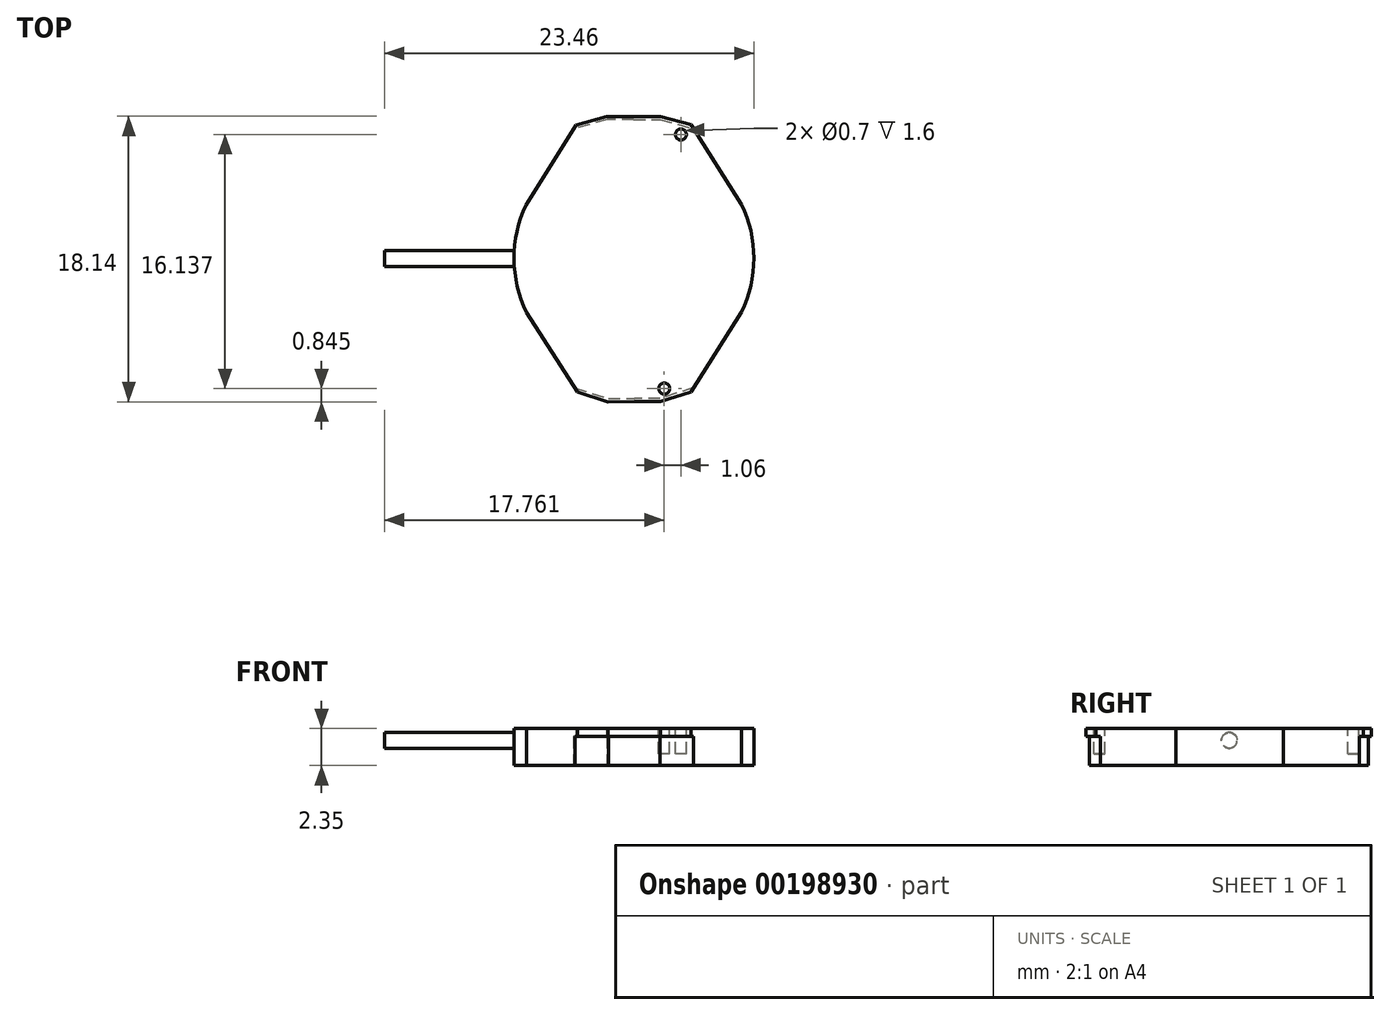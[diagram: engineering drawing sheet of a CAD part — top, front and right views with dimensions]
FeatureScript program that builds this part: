
annotation { "Feature Type Name" : "Feature", "Feature Type Description" : "" }
export const myFeature = defineFeature(function(context is Context, id is Id, definition is map)
    precondition{}
    {
        {
            var Q0;
            Q0=qCreatedBy(makeId("Top.planeOp"),FACE);
            var sketch = newSketch(context, id + "F0", { "sketchPlane" : qUnion([Q0])});
            skLineSegment(sketch, "E0", {"start": v(0, 0) * mm, "end": v(0, 18.2) * mm, "construction": true});
            skLineSegment(sketch, "E1", {"start": v(10.82, 18.2) * mm, "end": v(12.53, 18.2) * mm});
            skLineSegment(sketch, "E2", {"start": v(12.53, 18.2) * mm, "end": v(14.46, 17.67) * mm});
            skLineSegment(sketch, "E3", {"start": v(14.46, 17.67) * mm, "end": v(17.68, 12.6) * mm});
            skLineSegment(sketch, "E4", {"start": v(17.68, 5.76) * mm, "end": v(14.46, 0.7) * mm});
            skLineSegment(sketch, "E5", {"start": v(14.46, 0.7) * mm, "end": v(12.53, 0.07) * mm});
            skLineSegment(sketch, "E6", {"start": v(12.53, 0.07) * mm, "end": v(10.86, 0.07) * mm});
            skPoint(sketch, "E7.end.orphan", {"position": v(9.1, 18.2) * mm});
            skArc(sketch, "E8", {"start": v(17.68, 5.76) * mm, "mid": v(18.46, 9.19) * mm, "end": v(17.68, 12.6) * mm});
            skLineSegment(sketch, "E9.MirrorCS", {"start": v(10.82, 18.2) * mm, "end": v(9.1, 18.2) * mm});
            skLineSegment(sketch, "E10.MirrorCS", {"start": v(9.1, 18.2) * mm, "end": v(7.17, 17.65) * mm});
            skLineSegment(sketch, "E11.MirrorCS", {"start": v(7.17, 17.65) * mm, "end": v(3.98, 12.57) * mm});
            skArc(sketch, "E12.MirrorCS", {"start": v(4.02, 5.73) * mm, "mid": v(3.22, 9.15) * mm, "end": v(3.98, 12.57) * mm});
            skLineSegment(sketch, "E13.MirrorCS", {"start": v(4.02, 5.73) * mm, "end": v(7.26, 0.68) * mm});
            skLineSegment(sketch, "E14.MirrorCS", {"start": v(7.26, 0.68) * mm, "end": v(9.2, 0.06) * mm});
            skLineSegment(sketch, "E15.MirrorCS", {"start": v(9.2, 0.06) * mm, "end": v(10.86, 0.07) * mm});
            skPoint(sketch, "E16.MirrorCS.end.orphan", {"position": v(4.02, 5.73) * mm});
            skPoint(sketch, "E16.MirrorCS.start.orphan", {"position": v(3.98, 12.57) * mm});
            skSolve(sketch);
        }
        {
            var Q0;
            Q0=makeQuery(id+"F0.imprint","IMPRINT",FACE,{"disambiguationData":[TD([[makeQuery(id+"F0.imprint","IMPRINT",EDGE,{"derivedFrom":sQuery(id+"F0.wireOp",EDGE,"E1")}),-1.0]])]});
            extrude(context, id + "F1", {"entities" : qUnion([Q0]), "depth" : 2.35 * mm});
        }
        {
            var Q0;
            Q0=qCreatedBy(makeId("Right.planeOp"),FACE);
            var sketch = newSketch(context, id + "F2", { "sketchPlane" : qUnion([Q0])});
            skLineSegment(sketch, "E17", {"start": v(9.16, 1.6) * mm, "end": v(9.16, 0) * mm, "construction": true});
            skLineSegment(sketch, "E18", {"start": v(0.06, 0) * mm, "end": v(9.16, 0) * mm});
            skCircle(sketch, "E19", {"center": v(9.16, 1.6) * mm, "radius": 0.5 * mm});
            skSolve(sketch);
        }
        {
            var Q0;
            Q0=makeQuery(id+"F2.imprint","IMPRINT",FACE,{"disambiguationData":[TD([[makeQuery(id+"F2.imprint","IMPRINT",EDGE,{"derivedFrom":sQuery(id+"F2.wireOp",EDGE,"E19")}),1.0]])]});
            extrude(context, id + "F3", {"entities" : qUnion([Q0]), "operationType" : NewBodyOperationType.ADD, "depth" : 5 * mm, "hasSecondDirection" : true, "secondDirectionOppositeDirection" : true, "secondDirectionDepth" : 5 * mm});
        }
        {
            var Q0;
            Q0=makeQuery(id+"F1.opExtrude","CAP_FACE",FACE,{"disambiguationData":[OSD([sQuery(id+"F0.wireOp",EDGE,"E1"),sQuery(id+"F0.wireOp",EDGE,"E2"),sQuery(id+"F0.wireOp",EDGE,"E3"),sQuery(id+"F0.wireOp",EDGE,"E4"),sQuery(id+"F0.wireOp",EDGE,"E5"),sQuery(id+"F0.wireOp",EDGE,"E6"),sQuery(id+"F0.wireOp",EDGE,"E8"),sQuery(id+"F0.wireOp",EDGE,"E9.MirrorCS"),sQuery(id+"F0.wireOp",EDGE,"E10.MirrorCS"),sQuery(id+"F0.wireOp",EDGE,"E11.MirrorCS"),sQuery(id+"F0.wireOp",EDGE,"E12.MirrorCS"),sQuery(id+"F0.wireOp",EDGE,"E13.MirrorCS"),sQuery(id+"F0.wireOp",EDGE,"E14.MirrorCS"),sQuery(id+"F0.wireOp",EDGE,"E15.MirrorCS")])],"isStart":true});
            var sketch = newSketch(context, id + "F4", { "sketchPlane" : qUnion([Q0])});
            skLineSegment(sketch, "E20", {"start": v(10.86, -0.07) * mm, "end": v(10.82, -18.2) * mm, "construction": true});
            skLineSegment(sketch, "E21.0", {"start": v(7.09, -0.95) * mm, "end": v(9.22, -0.26) * mm});
            skLineSegment(sketch, "E21.1", {"start": v(9.22, -0.26) * mm, "end": v(10.86, -0.27) * mm});
            skLineSegment(sketch, "E21.2", {"start": v(12.5, -0.27) * mm, "end": v(10.86, -0.27) * mm});
            skLineSegment(sketch, "E21.3", {"start": v(14.63, -0.97) * mm, "end": v(12.5, -0.27) * mm});
            skLineSegment(sketch, "E22.0", {"start": v(9.13, -18) * mm, "end": v(7.02, -17.4) * mm});
            skLineSegment(sketch, "E22.1", {"start": v(10.82, -18) * mm, "end": v(9.13, -18) * mm});
            skLineSegment(sketch, "E22.2", {"start": v(10.82, -18) * mm, "end": v(12.5, -18) * mm});
            skLineSegment(sketch, "E22.3", {"start": v(12.5, -18) * mm, "end": v(14.62, -17.42) * mm});
            skSolve(sketch);
        }
        {
            var Q0;
            {var subQ2=sQuery(id+"F4.wireOp",EDGE,"E21.0");Q0=makeQuery(id+"F4.imprint","IMPRINT",FACE,{"disambiguationData":[TD([[makeQuery(id+"F4.imprint","IMPRINT",EDGE,{"derivedFrom":subQ2}),1.0]])]});}
            var Q1;
            {var subQ1=sQuery(id+"F4.wireOp",EDGE,"E22.0");Q1=makeQuery(id+"F4.imprint","IMPRINT",FACE,{"disambiguationData":[TD([[makeQuery(id+"F4.imprint","IMPRINT",EDGE,{"derivedFrom":subQ1}),1.0]])]});}
            extrude(context, id + "F5", {"entities" : qUnion([Q0, Q1]), "operationType" : NewBodyOperationType.REMOVE, "oppositeDirection" : true, "depth" : 1.85 * mm});
        }
        {
            var Q0;
            Q0=makeQuery(id+"F1.opExtrude","CAP_FACE",FACE,{"disambiguationData":[OSD([sQuery(id+"F0.wireOp",EDGE,"E1"),sQuery(id+"F0.wireOp",EDGE,"E2"),sQuery(id+"F0.wireOp",EDGE,"E3"),sQuery(id+"F0.wireOp",EDGE,"E4"),sQuery(id+"F0.wireOp",EDGE,"E5"),sQuery(id+"F0.wireOp",EDGE,"E6"),sQuery(id+"F0.wireOp",EDGE,"E8"),sQuery(id+"F0.wireOp",EDGE,"E9.MirrorCS"),sQuery(id+"F0.wireOp",EDGE,"E10.MirrorCS"),sQuery(id+"F0.wireOp",EDGE,"E11.MirrorCS"),sQuery(id+"F0.wireOp",EDGE,"E12.MirrorCS"),sQuery(id+"F0.wireOp",EDGE,"E13.MirrorCS"),sQuery(id+"F0.wireOp",EDGE,"E14.MirrorCS"),sQuery(id+"F0.wireOp",EDGE,"E15.MirrorCS")])],"isStart":false});
            var sketch = newSketch(context, id + "F6", { "sketchPlane" : qUnion([Q0])});
            skLineSegment(sketch, "E23", {"start": v(10.82, 18.2) * mm, "end": v(10.86, 0.07) * mm, "construction": true});
            skLineSegment(sketch, "E24", {"start": v(10.84, 9.13) * mm, "end": v(10.86, 0.9) * mm, "construction": true});
            skLineSegment(sketch, "E25", {"start": v(10.86, 0.9) * mm, "end": v(12.76, 0.9) * mm, "construction": true});
            skLineSegment(sketch, "E26", {"start": v(10.84, 9.13) * mm, "end": v(10.82, 17.03) * mm, "construction": true});
            skLineSegment(sketch, "E27", {"start": v(10.82, 17.03) * mm, "end": v(13.82, 17.04) * mm, "construction": true});
            skCircle(sketch, "E28", {"center": v(12.76, 0.9) * mm, "radius": 0.35 * mm});
            skCircle(sketch, "E29", {"center": v(13.82, 17.04) * mm, "radius": 0.35 * mm});
            skSolve(sketch);
        }
        {
            var Q0;
            Q0=makeQuery(id+"F6.imprint","IMPRINT",FACE,{"disambiguationData":[TD([[makeQuery(id+"F6.imprint","IMPRINT",EDGE,{"derivedFrom":sQuery(id+"F6.wireOp",EDGE,"E28")}),1.0]])]});
            var Q1;
            Q1=makeQuery(id+"F6.imprint","IMPRINT",FACE,{"disambiguationData":[TD([[makeQuery(id+"F6.imprint","IMPRINT",EDGE,{"derivedFrom":sQuery(id+"F6.wireOp",EDGE,"E29")}),1.0]])]});
            extrude(context, id + "F7", {"entities" : qUnion([Q0, Q1]), "operationType" : NewBodyOperationType.REMOVE, "oppositeDirection" : true, "depth" : 1.6 * mm});
        }
    });
